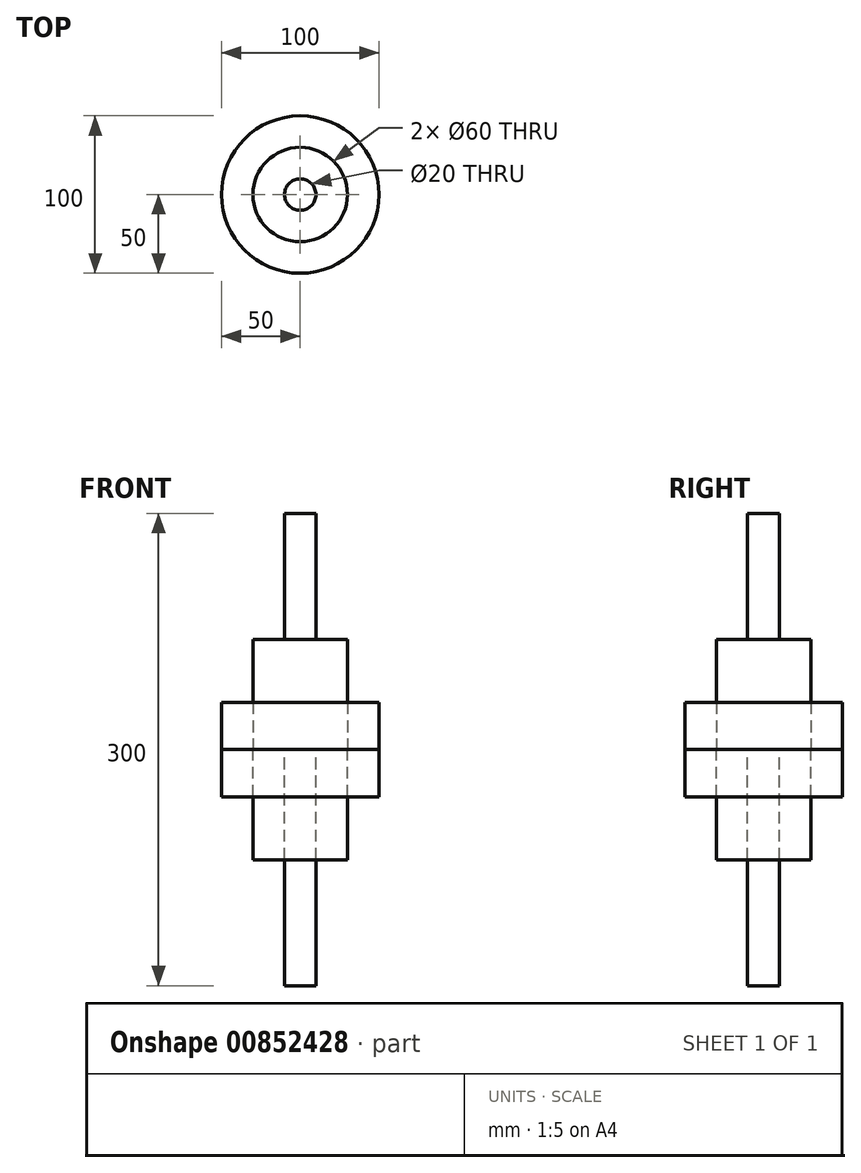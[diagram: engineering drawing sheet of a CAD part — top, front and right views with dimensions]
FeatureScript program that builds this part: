
annotation { "Feature Type Name" : "Feature", "Feature Type Description" : "" }
export const myFeature = defineFeature(function(context is Context, id is Id, definition is map)
    precondition{}
    {
        {
            var Q0;
            Q0=qCreatedBy(makeId("Top.planeOp"),FACE);
            var sketch = newSketch(context, id + "F0", { "sketchPlane" : qUnion([Q0])});
            skCircle(sketch, "E0", {"center": v(0, 0) * mm, "radius": 10 * mm});
            skCircle(sketch, "E1", {"center": v(0, 0) * mm, "radius": 30 * mm});
            skCircle(sketch, "E2", {"center": v(0, 0) * mm, "radius": 50 * mm});
            skSolve(sketch);
        }
        {
            var Q0;
            Q0=makeQuery(id+"F0.imprint","IMPRINT",FACE,{"disambiguationData":[TD([[makeQuery(id+"F0.imprint","IMPRINT",EDGE,{"derivedFrom":sQuery(id+"F0.wireOp",EDGE,"E0")}),1.0]])]});
            extrude(context, id + "F1", {"entities" : qUnion([Q0]), "depth" : 150 * mm, "offsetDistance" : 25 * mm});
        }
        {
            var Q0;
            Q0=makeQuery(id+"F0.imprint","IMPRINT",FACE,{"disambiguationData":[TD([[makeQuery(id+"F0.imprint","IMPRINT",EDGE,{"derivedFrom":sQuery(id+"F0.wireOp",EDGE,"E1")}),-1.0]])]});
            extrude(context, id + "F2", {"entities" : qUnion([Q0]), "depth" : 30 * mm, "offsetDistance" : 25 * mm});
        }
        {
            var Q0;
            Q0=makeQuery(id+"F0.imprint","IMPRINT",FACE,{"disambiguationData":[TD([[makeQuery(id+"F0.imprint","IMPRINT",EDGE,{"derivedFrom":sQuery(id+"F0.wireOp",EDGE,"E0")}),-1.0]])]});
            extrude(context, id + "F3", {"entities" : qUnion([Q0]), "depth" : 70 * mm, "offsetDistance" : 25 * mm});
        }
        {
            var Q0;
            Q0=makeQuery(id+"F0.imprint","IMPRINT",FACE,{"disambiguationData":[TD([[makeQuery(id+"F0.imprint","IMPRINT",EDGE,{"derivedFrom":sQuery(id+"F0.wireOp",EDGE,"E0")}),1.0]])]});
            extrude(context, id + "F4", {"entities" : qUnion([Q0]), "operationType" : NewBodyOperationType.ADD, "oppositeDirection" : true, "depth" : 150 * mm, "offsetDistance" : 25 * mm});
        }
        {
            var Q0;
            Q0=makeQuery(id+"F0.imprint","IMPRINT",FACE,{"disambiguationData":[TD([[makeQuery(id+"F0.imprint","IMPRINT",EDGE,{"derivedFrom":sQuery(id+"F0.wireOp",EDGE,"E0")}),-1.0]])]});
            extrude(context, id + "F5", {"entities" : qUnion([Q0]), "oppositeDirection" : true, "depth" : 70 * mm, "offsetDistance" : 25 * mm});
        }
        {
            var Q0;
            Q0=makeQuery(id+"F0.imprint","IMPRINT",FACE,{"disambiguationData":[TD([[makeQuery(id+"F0.imprint","IMPRINT",EDGE,{"derivedFrom":sQuery(id+"F0.wireOp",EDGE,"E1")}),-1.0]])]});
            extrude(context, id + "F6", {"entities" : qUnion([Q0]), "oppositeDirection" : true, "depth" : 30 * mm, "offsetDistance" : 25 * mm});
        }
    });
